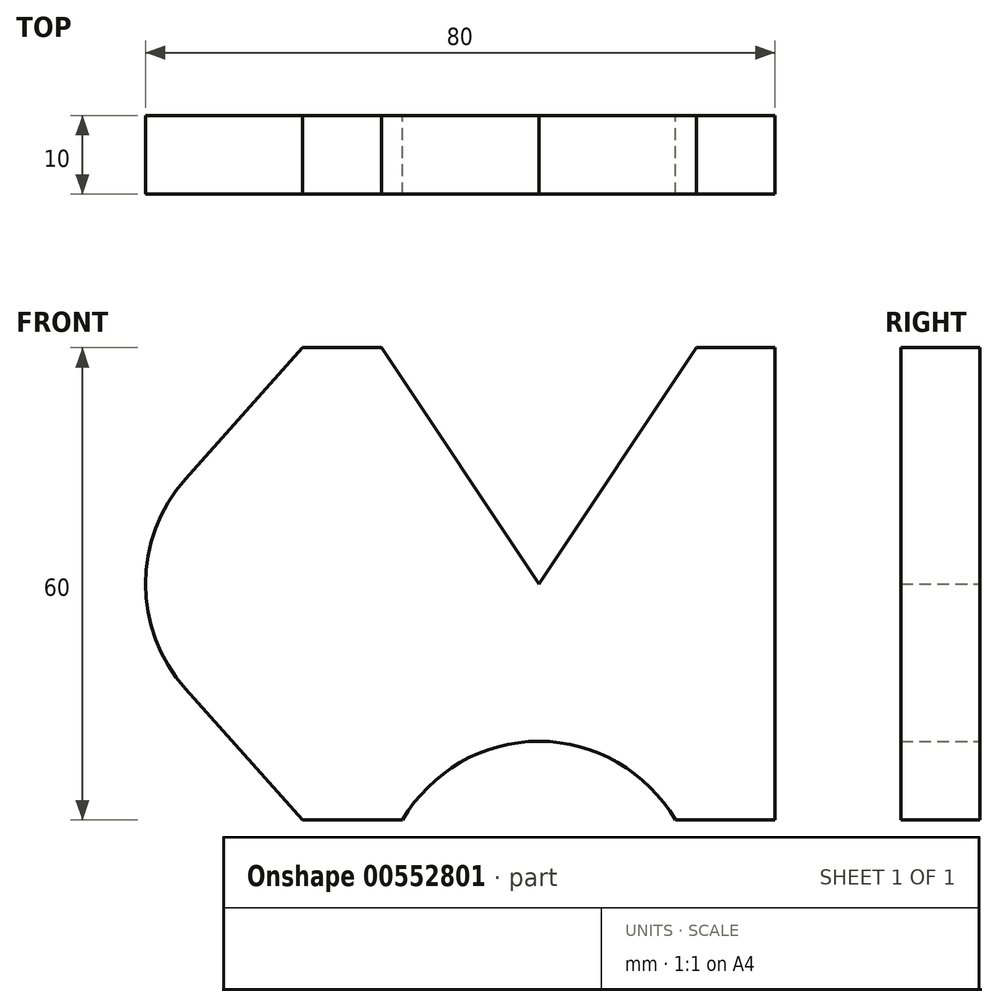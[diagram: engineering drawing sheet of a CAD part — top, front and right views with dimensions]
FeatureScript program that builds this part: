
annotation { "Feature Type Name" : "Feature", "Feature Type Description" : "" }
export const myFeature = defineFeature(function(context is Context, id is Id, definition is map)
    precondition{}
    {
        {
            var Q0;
            Q0=qCreatedBy(makeId("Front.planeOp"),FACE);
            var sketch = newSketch(context, id + "F0", { "sketchPlane" : qUnion([Q0])});
            skLineSegment(sketch, "E0", {"start": v(0, 0) * mm, "end": v(20, 30) * mm});
            skLineSegment(sketch, "E1", {"start": v(20, 30) * mm, "end": v(30, 30) * mm});
            skLineSegment(sketch, "E2", {"start": v(30, 30) * mm, "end": v(30, -30) * mm});
            skLineSegment(sketch, "E3", {"start": v(30, -30) * mm, "end": v(17.32, -30) * mm});
            skArc(sketch, "E4", {"start": v(17.32, -30) * mm, "mid": v(0, -20) * mm, "end": v(-17.32, -30) * mm});
            skLineSegment(sketch, "E5", {"start": v(-17.32, -30) * mm, "end": v(-30, -30) * mm});
            skLineSegment(sketch, "E6", {"start": v(-30, -30) * mm, "end": v(-44.9, -13.33) * mm});
            skLineSegment(sketch, "E7", {"start": v(0, 0) * mm, "end": v(-20, 30) * mm});
            skLineSegment(sketch, "E8", {"start": v(-20, 30) * mm, "end": v(-30, 30) * mm});
            skLineSegment(sketch, "E9", {"start": v(-30, 30) * mm, "end": v(-44.9, 13.33) * mm});
            skArc(sketch, "E10", {"start": v(-44.9, 13.33) * mm, "mid": v(-50, 0) * mm, "end": v(-44.9, -13.33) * mm});
            skLineSegment(sketch, "E11", {"start": v(-30, 30) * mm, "end": v(-30, -30) * mm, "construction": true});
            skSolve(sketch);
        }
        {
            var Q0;
            Q0=makeQuery(id+"F0.imprint","IMPRINT",FACE,{"disambiguationData":[TD([[makeQuery(id+"F0.imprint","IMPRINT",EDGE,{"derivedFrom":sQuery(id+"F0.wireOp",EDGE,"E0")}),-1.0]])]});
            extrude(context, id + "F1", {"entities" : qUnion([Q0]), "depth" : 10 * mm, "offsetDistance" : 25 * mm});
        }
    });
